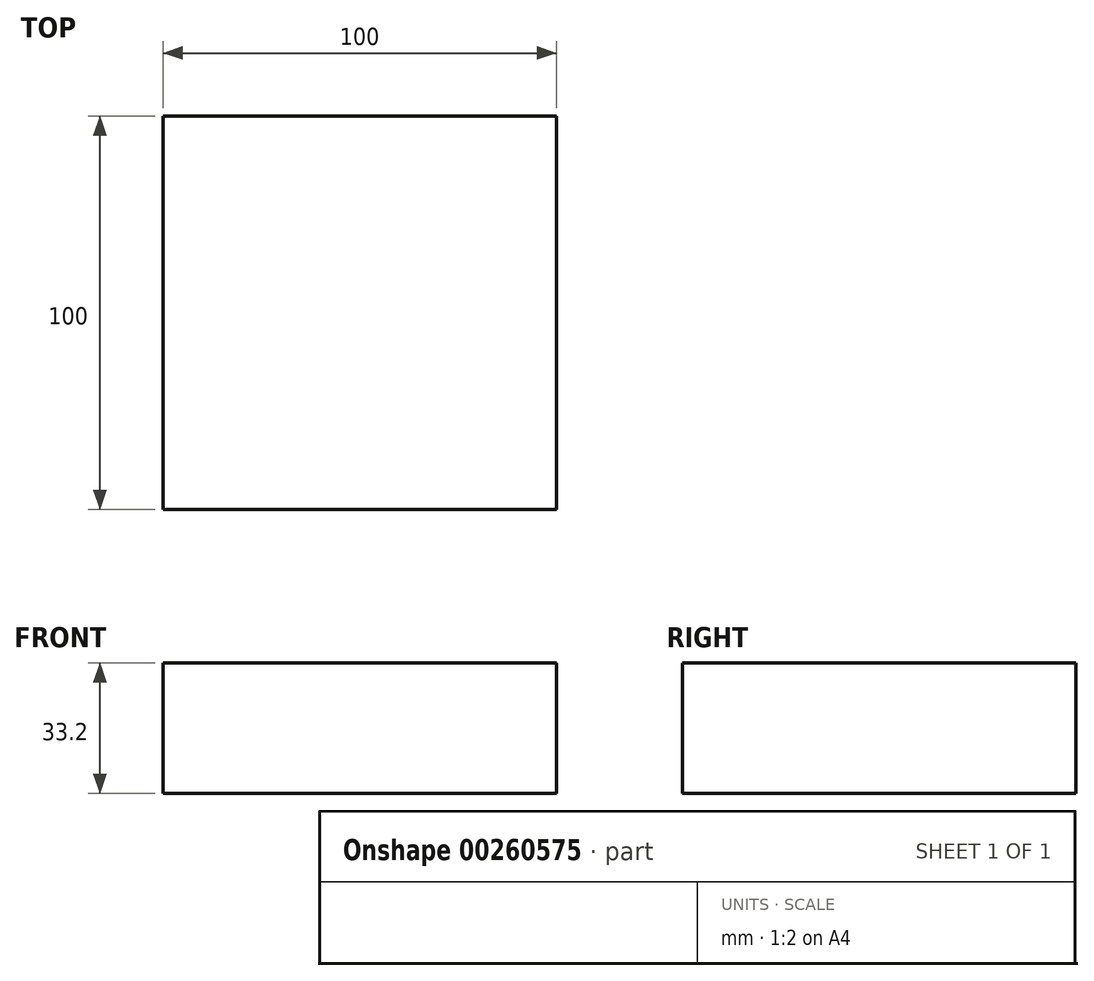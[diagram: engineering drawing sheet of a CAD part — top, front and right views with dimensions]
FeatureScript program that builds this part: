
annotation { "Feature Type Name" : "Feature", "Feature Type Description" : "" }
export const myFeature = defineFeature(function(context is Context, id is Id, definition is map)
    precondition{}
    {
        {
            var Q0;
            Q0=qCreatedBy(makeId("Top.planeOp"),FACE);
            var sketch = newSketch(context, id + "F0", { "sketchPlane" : qUnion([Q0])});
            skLineSegment(sketch, "E0.bottom", {"start": v(-50, 50) * mm, "end": v(50, 50) * mm});
            skLineSegment(sketch, "E0.top", {"start": v(-50, -50) * mm, "end": v(50, -50) * mm});
            skLineSegment(sketch, "E0.left", {"start": v(-50, 50) * mm, "end": v(-50, -50) * mm});
            skLineSegment(sketch, "E0.right", {"start": v(50, 50) * mm, "end": v(50, -50) * mm});
            skPoint(sketch, "E0.middle", {"position": v(0, 0) * mm});
            skSolve(sketch);
        }
        {
            var Q0;
            Q0=makeQuery(id+"F0.imprint","IMPRINT",FACE,{"disambiguationData":[TD([[makeQuery(id+"F0.imprint","IMPRINT",EDGE,{"derivedFrom":sQuery(id+"F0.wireOp",EDGE,"E0.bottom")}),-1.0]])]});
            extrude(context, id + "F1", {"entities" : qUnion([Q0]), "oppositeDirection" : true, "depth" : 33.2 * mm});
        }
    });
